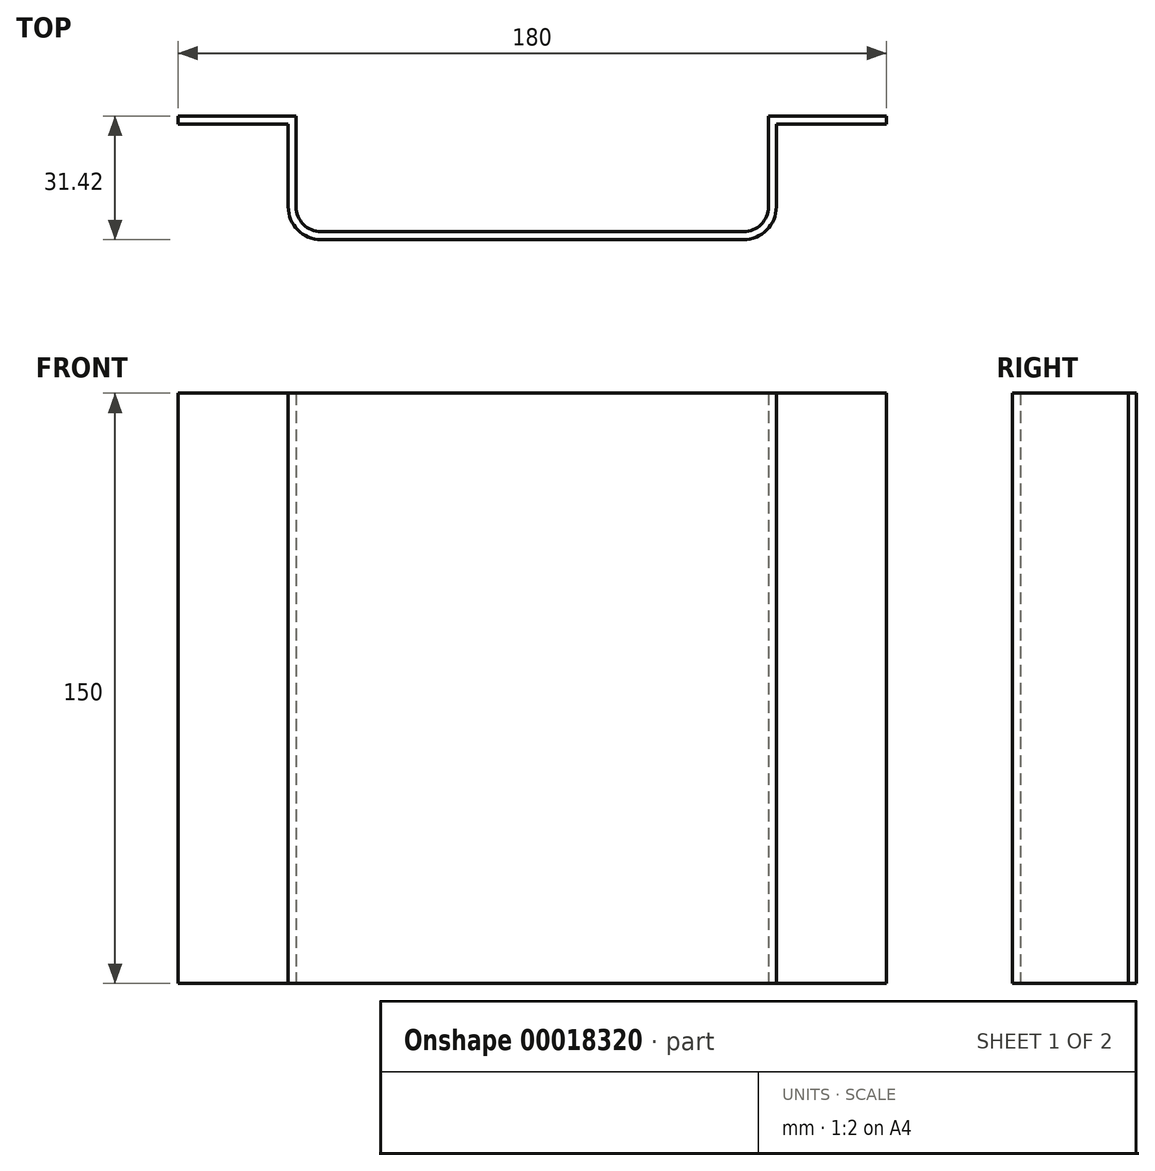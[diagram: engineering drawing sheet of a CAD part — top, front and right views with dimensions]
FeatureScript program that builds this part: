
annotation { "Feature Type Name" : "Feature", "Feature Type Description" : "" }
export const myFeature = defineFeature(function(context is Context, id is Id, definition is map)
    precondition{}
    {
        {
            var Q0;
            Q0=qCreatedBy(makeId("Top.planeOp"),FACE);
            var sketch = newSketch(context, id + "F0", { "sketchPlane" : qUnion([Q0])});
            skLineSegment(sketch, "E0", {"start": v(-72.58, 29.42) * mm, "end": v(-42.58, 29.42) * mm});
            skLineSegment(sketch, "E1", {"start": v(-42.58, 29.42) * mm, "end": v(-42.58, 6.35) * mm});
            skLineSegment(sketch, "E2", {"start": v(-36.23, 0) * mm, "end": v(71.07, 0) * mm});
            skLineSegment(sketch, "E3", {"start": v(77.42, 6.35) * mm, "end": v(77.42, 29.42) * mm});
            skLineSegment(sketch, "E4", {"start": v(77.42, 29.42) * mm, "end": v(107.42, 29.42) * mm});
            skPoint(sketch, "E5.visualSharp", {"position": v(-42.58, 0) * mm});
            skArc(sketch, "E5.filletArc", {"start": v(-42.58, 6.35) * mm, "mid": v(-40.72, 1.86) * mm, "end": v(-36.23, 0) * mm});
            skPoint(sketch, "E6.visualSharp", {"position": v(77.42, 0) * mm});
            skArc(sketch, "E6.filletArc", {"start": v(71.07, 0) * mm, "mid": v(75.56, 1.86) * mm, "end": v(77.42, 6.35) * mm});
            skLineSegment(sketch, "E7.0", {"start": v(79.42, 27.42) * mm, "end": v(107.42, 27.42) * mm});
            skLineSegment(sketch, "E7.1", {"start": v(79.42, 6.35) * mm, "end": v(79.42, 27.42) * mm});
            skArc(sketch, "E7.2", {"start": v(71.07, -2) * mm, "mid": v(76.97, 0.45) * mm, "end": v(79.42, 6.35) * mm});
            skLineSegment(sketch, "E7.3", {"start": v(-36.23, -2) * mm, "end": v(71.07, -2) * mm});
            skArc(sketch, "E7.4", {"start": v(-44.58, 6.35) * mm, "mid": v(-42.14, 0.45) * mm, "end": v(-36.23, -2) * mm});
            skLineSegment(sketch, "E7.5", {"start": v(-44.58, 27.42) * mm, "end": v(-44.58, 6.35) * mm});
            skLineSegment(sketch, "E7.6", {"start": v(-72.58, 27.42) * mm, "end": v(-44.58, 27.42) * mm});
            skLineSegment(sketch, "E8", {"start": v(-72.58, 29.42) * mm, "end": v(-72.58, 27.42) * mm});
            skLineSegment(sketch, "E9", {"start": v(107.42, 29.42) * mm, "end": v(107.42, 27.42) * mm});
            skSolve(sketch);
        }
        {
            var Q0;
            Q0 = qSketchRegion(id + "F0", true);
            extrude(context, id + "F1", {"entities" : qUnion([Q0]), "depth" : 150 * mm});
        }
        {
            var Q0;
            Q0 = qSketchRegion(id + "F0", true);
            extrude(context, id + "F2", {"entities" : qUnion([Q0]), "operationType" : NewBodyOperationType.ADD, "depth" : 100 * mm});
        }
    });
